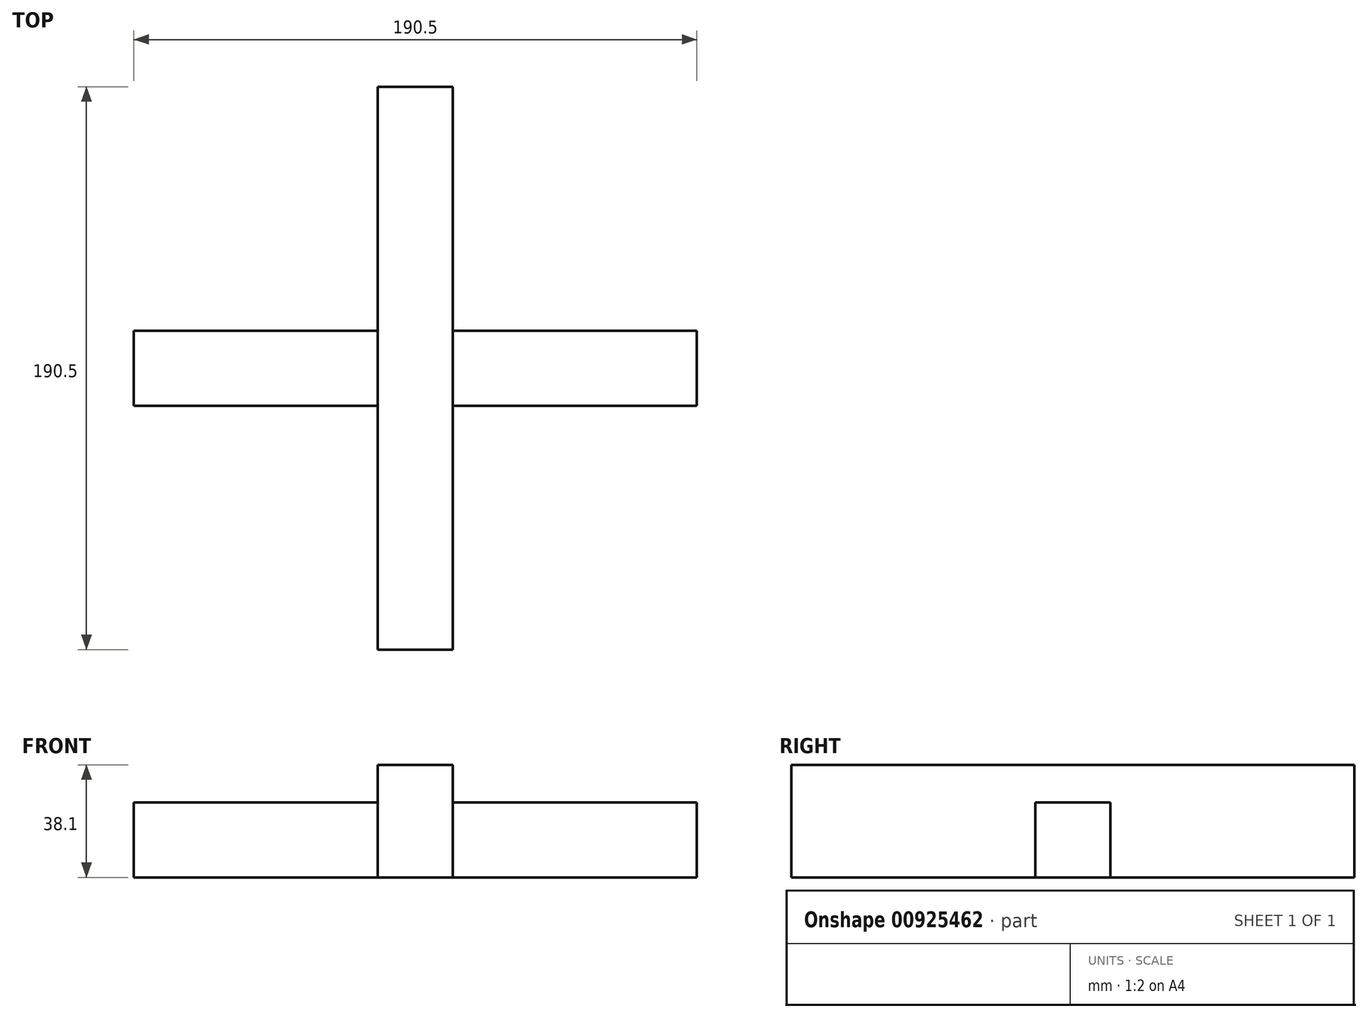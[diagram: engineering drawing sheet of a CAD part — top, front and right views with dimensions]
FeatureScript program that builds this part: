
annotation { "Feature Type Name" : "Feature", "Feature Type Description" : "" }
export const myFeature = defineFeature(function(context is Context, id is Id, definition is map)
    precondition{}
    {
        {
            var Q0;
            Q0=qCreatedBy(makeId("Top.planeOp"),FACE);
            var sketch = newSketch(context, id + "F0", { "sketchPlane" : qUnion([Q0])});
            skLineSegment(sketch, "E0.bottom", {"start": v(-12.7, 95.25) * mm, "end": v(12.7, 95.25) * mm});
            skLineSegment(sketch, "E0.top", {"start": v(-12.7, -95.25) * mm, "end": v(12.7, -95.25) * mm});
            skLineSegment(sketch, "E0.left", {"start": v(-12.7, 95.25) * mm, "end": v(-12.7, -95.25) * mm});
            skLineSegment(sketch, "E0.right", {"start": v(12.7, 95.25) * mm, "end": v(12.7, -95.25) * mm});
            skPoint(sketch, "E0.middle", {"position": v(0, 0) * mm});
            skLineSegment(sketch, "E1.bottom", {"start": v(95.25, -12.7) * mm, "end": v(-95.25, -12.7) * mm});
            skLineSegment(sketch, "E1.top", {"start": v(95.25, 12.7) * mm, "end": v(-95.25, 12.7) * mm});
            skLineSegment(sketch, "E1.left", {"start": v(95.25, -12.7) * mm, "end": v(95.25, 12.7) * mm});
            skLineSegment(sketch, "E1.right", {"start": v(-95.25, -12.7) * mm, "end": v(-95.25, 12.7) * mm});
            skSolve(sketch);
        }
        {
            var Q0;
            {var subQ0=sQuery(id+"F0.wireOp",EDGE,"E0.bottom");Q0=makeQuery(id+"F0.imprint","IMPRINT",FACE,{"disambiguationData":[TD([[makeQuery(id+"F0.imprint","IMPRINT",EDGE,{"derivedFrom":subQ0}),-1.0]])]});}
            var Q1;
            {var subQ0=sQuery(id+"F0.wireOp",EDGE,"E1.top");var subQ1=sQuery(id+"F0.wireOp",EDGE,"E0.left");var subQ2=makeQuery(id+"F0.imprint","INTERSECT",VERTEX,{"derivedFrom":[subQ1,subQ0]});Q1=makeQuery(id+"F0.imprint","IMPRINT",FACE,{"disambiguationData":[TD([[makeQuery(id+"F0.imprint","IMPRINT",EDGE,{"disambiguationData":[TD([[subQ2,-1.0]])],"derivedFrom":subQ1}),1.0]])]});}
            var Q2;
            {var subQ0=sQuery(id+"F0.wireOp",EDGE,"E0.top");Q2=makeQuery(id+"F0.imprint","IMPRINT",FACE,{"disambiguationData":[TD([[makeQuery(id+"F0.imprint","IMPRINT",EDGE,{"derivedFrom":subQ0}),1.0]])]});}
            extrude(context, id + "F1", {"entities" : qUnion([Q0, Q1, Q2]), "depth" : 25.4 * mm, "offsetDistance" : 25.4 * mm});
        }
        {
            var Q0;
            Q0 = qSketchRegion(id + "F0", true);
            extrude(context, id + "F2", {"entities" : qUnion([Q0]), "operationType" : NewBodyOperationType.ADD, "endBound" : BoundingType.SYMMETRIC, "depth" : 25.4 * mm, "offsetDistance" : 25.4 * mm});
        }
    });
